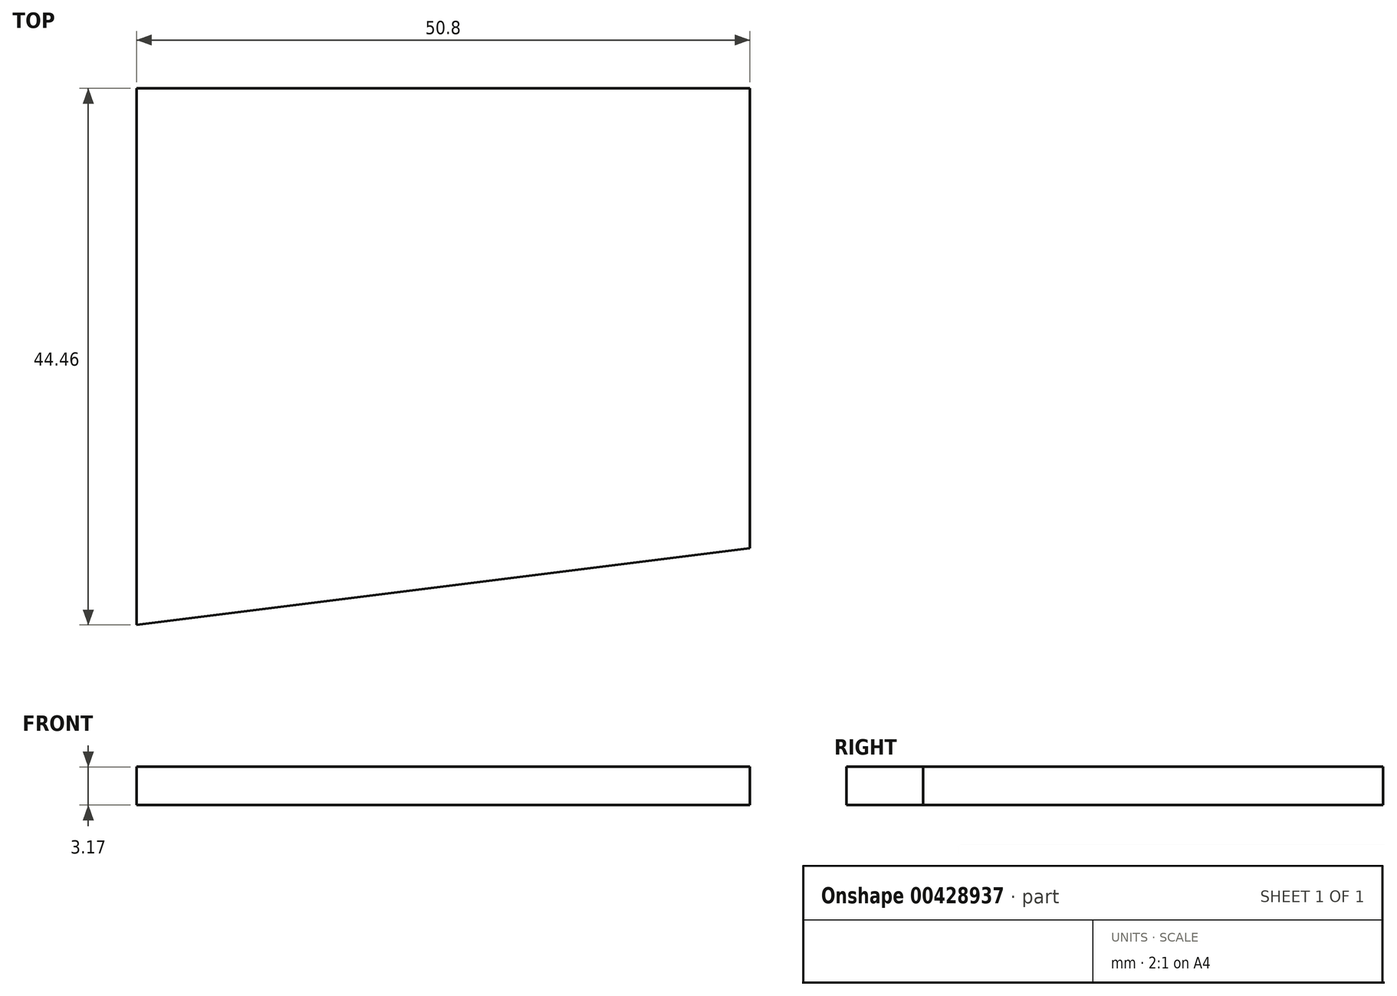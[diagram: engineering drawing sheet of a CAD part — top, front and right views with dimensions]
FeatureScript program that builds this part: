
annotation { "Feature Type Name" : "Feature", "Feature Type Description" : "" }
export const myFeature = defineFeature(function(context is Context, id is Id, definition is map)
    precondition{}
    {
        {
            var Q0;
            Q0=qCreatedBy(makeId("Top.planeOp"),FACE);
            var sketch = newSketch(context, id + "F0", { "sketchPlane" : qUnion([Q0])});
            skLineSegment(sketch, "E0.bottom", {"start": v(-57.15, -3.18) * mm, "end": v(-6.35, -3.18) * mm});
            skLineSegment(sketch, "E0.left", {"start": v(-57.15, -3.18) * mm, "end": v(-57.15, -47.63) * mm});
            skLineSegment(sketch, "E1", {"start": v(-6.35, -3.18) * mm, "end": v(-6.35, -41.28) * mm});
            skLineSegment(sketch, "E2", {"start": v(-57.15, -47.63) * mm, "end": v(-6.35, -41.28) * mm});
            skSolve(sketch);
        }
        {
            var Q0;
            Q0=makeQuery(id+"F0.imprint","IMPRINT",FACE,{"disambiguationData":[TD([[makeQuery(id+"F0.imprint","IMPRINT",EDGE,{"derivedFrom":sQuery(id+"F0.wireOp",EDGE,"E0.bottom")}),-1.0]])]});
            extrude(context, id + "F1", {"entities" : qUnion([Q0]), "depth" : 3.17 * mm});
        }
        {
            var Q0;
            Q0=makeQuery(id+"F1.opExtrude","CAP_FACE",FACE,{"disambiguationData":[OSD([sQuery(id+"F0.wireOp",EDGE,"E0.bottom"),sQuery(id+"F0.wireOp",EDGE,"E0.left"),sQuery(id+"F0.wireOp",EDGE,"E1"),sQuery(id+"F0.wireOp",EDGE,"E2")])],"isStart":false});
            var sketch = newSketch(context, id + "F2", { "sketchPlane" : qUnion([Q0])});
            skText(sketch, "E3", { "text": "Plead the 2nd", "fontName": "OpenSans-Italic.ttf"});
            const initialGuessF2  = {"E3": [-0.02232, 0.01193, 1, 0, 0.0052]};
            skSetInitialGuess(sketch, initialGuessF2);
            skSolve(sketch);
        }
        {
            var Q0;
            Q0 = qSketchRegion(id + "F2", true);
            extrude(context, id + "F3", {"entities" : qUnion([Q0]), "operationType" : NewBodyOperationType.REMOVE, "oppositeDirection" : true, "depth" : 0.08 * mm});
        }
        {
            var Q0;
            {var subQ0=sQuery(id+"F0.wireOp",EDGE,"E0.left");var subQ1=sQuery(id+"F0.wireOp",EDGE,"E2");var subQ2=sQuery(id+"F0.wireOp",EDGE,"E0.bottom");var subQ3=sQuery(id+"F0.wireOp",EDGE,"E1");Q0=makeQuery(id+"F3.boolean.opBoolean","SPLIT",FACE,{"disambiguationData":[TD([makeQuery(id+"F1.opExtrude","SWEPT_FACE",FACE,{"disambiguationData":[OSD([subQ2])]})])],"derivedFrom":makeQuery(id+"F1.opExtrude","CAP_FACE",FACE,{"disambiguationData":[OSD([subQ2,subQ0,subQ3,subQ1])],"isStart":false})});}
            var sketch = newSketch(context, id + "F4", { "sketchPlane" : qUnion([Q0])});
            skText(sketch, "E4", { "text": "001", "fontName": "OpenSans-Italic.ttf"});
            const initialGuessF4  = {"E4": [0.01289, 0.00472, 1, 0, 0.003]};
            skSetInitialGuess(sketch, initialGuessF4);
            skSolve(sketch);
        }
        {
            var Q0;
            Q0 = qSketchRegion(id + "F4", true);
            extrude(context, id + "F5", {"entities" : qUnion([Q0]), "operationType" : NewBodyOperationType.REMOVE, "oppositeDirection" : true, "depth" : 0.08 * mm});
        }
    });
